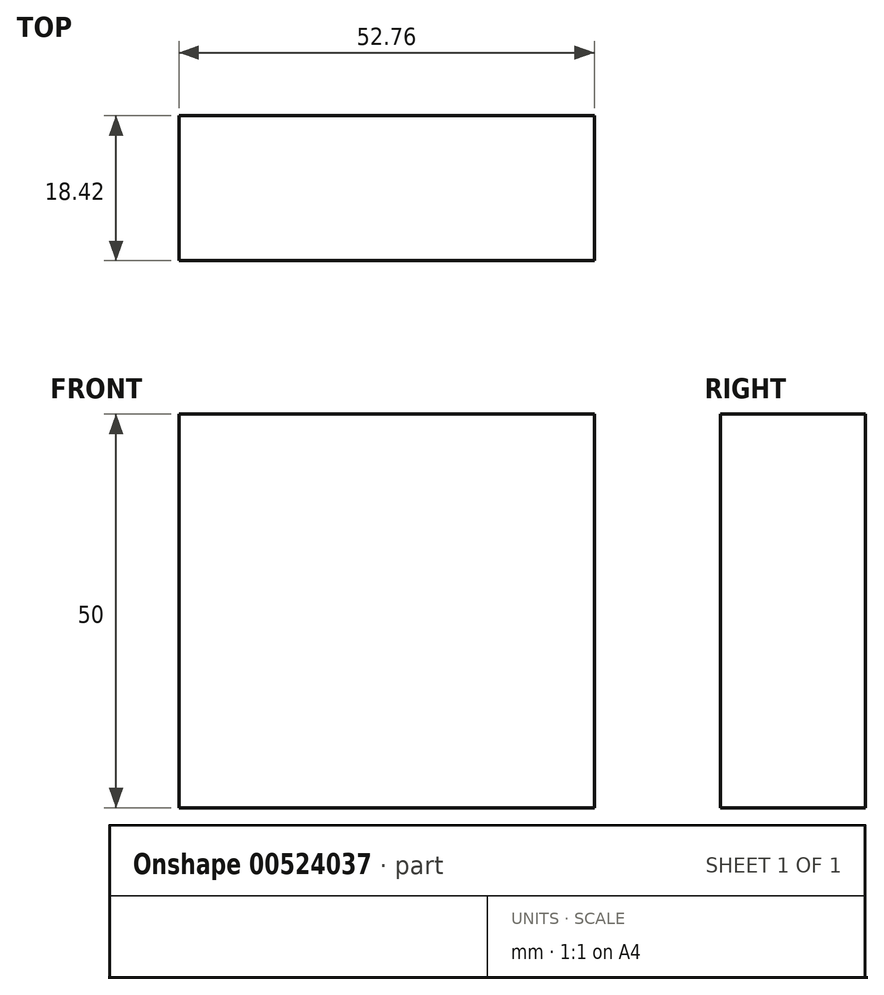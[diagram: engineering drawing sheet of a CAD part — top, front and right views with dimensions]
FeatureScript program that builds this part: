
annotation { "Feature Type Name" : "Feature", "Feature Type Description" : "" }
export const myFeature = defineFeature(function(context is Context, id is Id, definition is map)
    precondition{}
    {
        {
            var Q0;
            Q0=qCreatedBy(makeId("Top.planeOp"),FACE);
            var sketch = newSketch(context, id + "F0", { "sketchPlane" : qUnion([Q0])});
            skLineSegment(sketch, "E0", {"start": v(-30.76, 0) * mm, "end": v(22, 0) * mm});
            skLineSegment(sketch, "E1", {"start": v(22, 0) * mm, "end": v(22, 18.42) * mm});
            skLineSegment(sketch, "E2", {"start": v(22, 18.42) * mm, "end": v(-30.76, 18.42) * mm});
            skLineSegment(sketch, "E3", {"start": v(-30.76, 18.42) * mm, "end": v(-30.76, 0) * mm});
            skSolve(sketch);
        }
        {
            var Q0;
            Q0=makeQuery(id+"F0.imprint","IMPRINT",FACE,{"disambiguationData":[TD([[makeQuery(id+"F0.imprint","IMPRINT",EDGE,{"derivedFrom":sQuery(id+"F0.wireOp",EDGE,"E0")}),1.0]])]});
            extrude(context, id + "F1", {"entities" : qUnion([Q0]), "depth" : 50 * mm, "offsetDistance" : 25 * mm});
        }
    });
